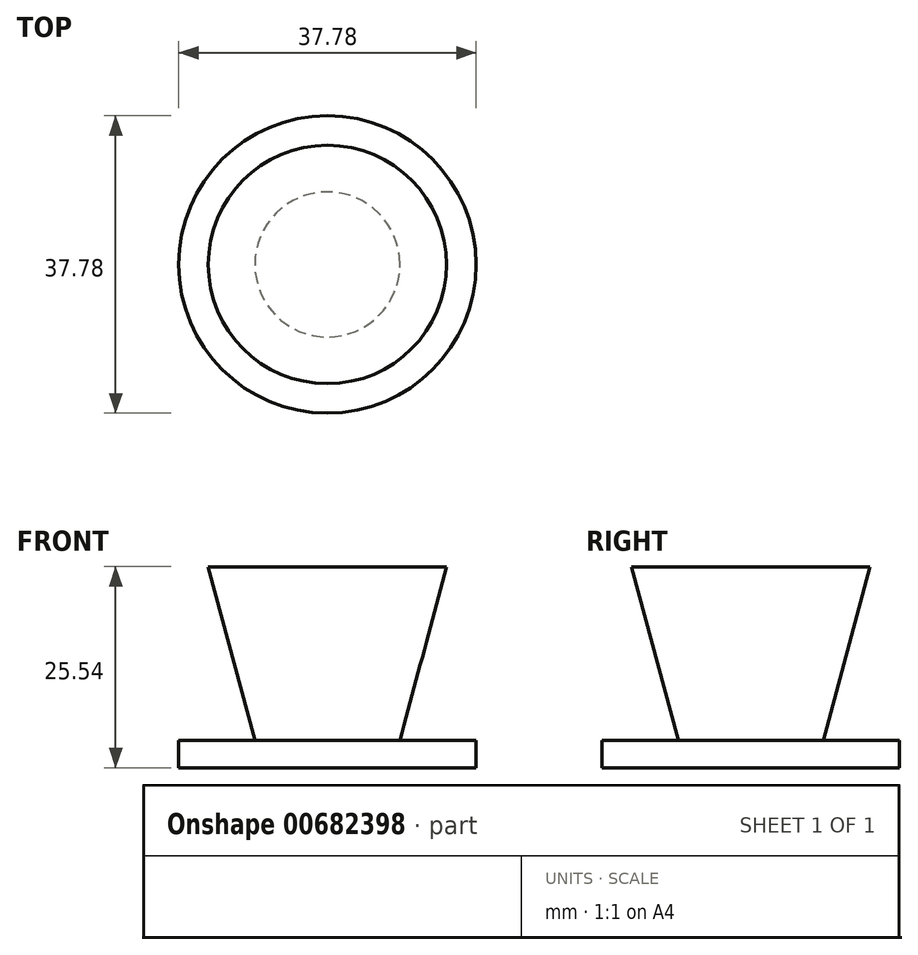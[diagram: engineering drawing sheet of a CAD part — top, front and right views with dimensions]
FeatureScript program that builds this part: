
annotation { "Feature Type Name" : "Feature", "Feature Type Description" : "" }
export const myFeature = defineFeature(function(context is Context, id is Id, definition is map)
    precondition{}
    {
        {
            var Q0;
            Q0=qCreatedBy(makeId("Right.planeOp"),FACE);
            var sketch = newSketch(context, id + "F0", { "sketchPlane" : qUnion([Q0])});
            skLineSegment(sketch, "E0.bottom", {"start": v(0, 0) * mm, "end": v(-18.9, 0) * mm});
            skLineSegment(sketch, "E0.top", {"start": v(0, 3.5) * mm, "end": v(-18.9, 3.5) * mm});
            skLineSegment(sketch, "E0.left", {"start": v(0, 0) * mm, "end": v(0, 3.5) * mm});
            skLineSegment(sketch, "E0.right", {"start": v(-18.9, 0) * mm, "end": v(-18.9, 3.5) * mm});
            skLineSegment(sketch, "E1", {"start": v(-9.22, 3.5) * mm, "end": v(-15.14, 25.54) * mm});
            skLineSegment(sketch, "E2", {"start": v(-15.14, 25.54) * mm, "end": v(0, 25.54) * mm});
            skLineSegment(sketch, "E3", {"start": v(0, 25.54) * mm, "end": v(0, 3.5) * mm});
            skSolve(sketch);
        }
        {
            var Q0;
            {var subQ2=sQuery(id+"F0.wireOp",EDGE,"E1");Q0=makeQuery(id+"F0.imprint","IMPRINT",FACE,{"disambiguationData":[TD([[makeQuery(id+"F0.imprint","IMPRINT",EDGE,{"derivedFrom":subQ2}),-1.0]])]});}
            var Q1;
            Q1=makeQuery(id+"F0.imprint","IMPRINT",FACE,{"disambiguationData":[TD([[makeQuery(id+"F0.imprint","IMPRINT",EDGE,{"derivedFrom":sQuery(id+"F0.wireOp",EDGE,"E0.bottom")}),-1.0]])]});
            var Q2;
            Q2=sQuery(id+"F0.wireOp",EDGE,"E3");
            revolve(context, id + "F1", {"entities" : qUnion([Q0, Q1]), "axis" : qUnion([Q2]), "revolveType" : RevolveType.FULL});
        }
    });
